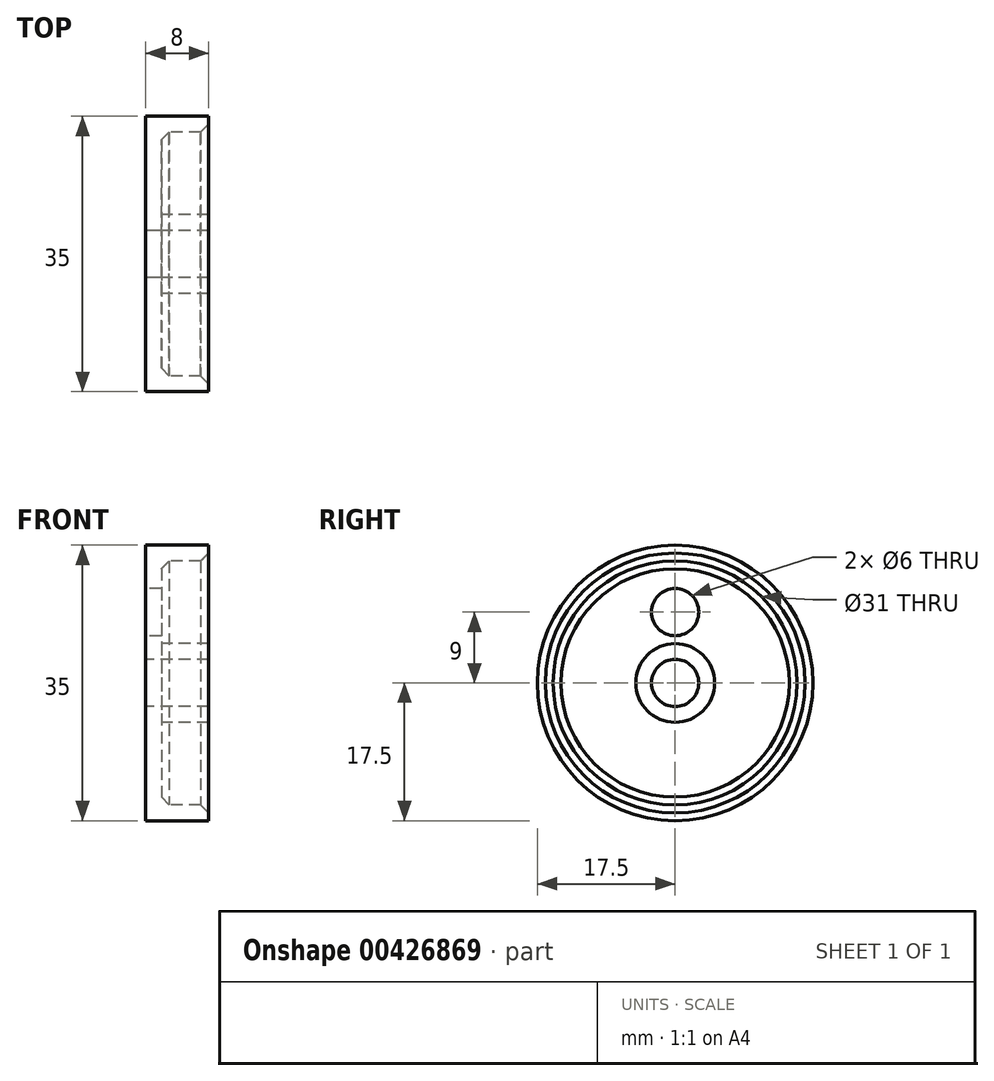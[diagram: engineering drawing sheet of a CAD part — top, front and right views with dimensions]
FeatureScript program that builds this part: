
annotation { "Feature Type Name" : "Feature", "Feature Type Description" : "" }
export const myFeature = defineFeature(function(context is Context, id is Id, definition is map)
    precondition{}
    {
        {
            var Q0;
            Q0=qCreatedBy(makeId("Top.planeOp"),FACE);
            var sketch = newSketch(context, id + "F0", { "sketchPlane" : qUnion([Q0])});
            skLineSegment(sketch, "E0.bottom", {"start": v(0, 0) * mm, "end": v(8, 0) * mm});
            skLineSegment(sketch, "E0.top", {"start": v(0, 17.5) * mm, "end": v(8, 17.5) * mm});
            skLineSegment(sketch, "E0.left", {"start": v(0, 0) * mm, "end": v(0, 17.5) * mm});
            skLineSegment(sketch, "E0.right", {"start": v(8, 0) * mm, "end": v(8, 17.5) * mm});
            skSolve(sketch);
        }
        {
            var Q0;
            Q0 = qSketchRegion(id + "F0", true);
            var Q1;
            Q1=sQuery(id+"F0.wireOp",EDGE,"E0.bottom");
            revolve(context, id + "F1", {"entities" : qUnion([Q0]), "axis" : qUnion([Q1]), "revolveType" : RevolveType.FULL});
        }
        {
            var Q0;
            Q0=qCreatedBy(makeId("Right.planeOp"),FACE);
            var sketch = newSketch(context, id + "F2", { "sketchPlane" : qUnion([Q0])});
            skPoint(sketch, "E1", {"position": v(0, 0) * mm});
            skSolve(sketch);
        }
        {
            var Q0;
            Q0=sQuery(id+"F2.wireOp",VERTEX,"E1");
            var Q1;
            Q1=makeQuery(id+"F1.opRevolve","SWEPT_BODY",BODY,{"disambiguationData":[OSD([sQuery(id+"F0.wireOp",EDGE,"E0.bottom"),sQuery(id+"F0.wireOp",EDGE,"E0.top"),sQuery(id+"F0.wireOp",EDGE,"E0.left"),sQuery(id+"F0.wireOp",EDGE,"E0.right")])]});
            hole(context, id + "F3", {"style" : HoleStyle.SIMPLE, "endStyle" : HoleEndStyle.THROUGH, "oppositeDirection" : true, "holeDiameter" : 6 * mm, "isTappedThrough" : true, "tappedDepth" : 12 * mm, "tapClearance" : 3, "locations" : qUnion([Q0]), "scope" : qUnion([Q1])});
        }
        {
            var Q0;
            Q0=makeQuery(id+"F1.opRevolve","SWEPT_FACE",FACE,{"disambiguationData":[OSD([sQuery(id+"F0.wireOp",EDGE,"E0.right")])]});
            shell(context, id + "F4", {"entities" : qUnion([Q0]), "thickness" : 2 * mm});
        }
        {
            var Q0;
            Q0=makeQuery(id+"F4.opShell","OFFSET_FACE",FACE,{"disambiguationData":[OSD([sQuery(id+"F0.wireOp",EDGE,"E0.top")])]});
            chamfer(context, id + "F5", {"entities" : qUnion([Q0]), "width" : 1 * mm, "tangentPropagation" : true});
        }
        {
            var Q0;
            Q0=qCreatedBy(makeId("Right.planeOp"),FACE);
            var sketch = newSketch(context, id + "F6", { "sketchPlane" : qUnion([Q0])});
            skPoint(sketch, "E2", {"position": v(22.4, 8.83) * mm});
            skCircle(sketch, "E3", {"center": v(0, 9) * mm, "radius": 2.06 * mm});
            skSolve(sketch);
        }
        {
            var Q0;
            Q0=sQuery(id+"F6.wireOp",VERTEX,"E3.center");
            var Q1;
            Q1=makeQuery(id+"F1.opRevolve","SWEPT_BODY",BODY,{"disambiguationData":[OSD([sQuery(id+"F0.wireOp",EDGE,"E0.bottom"),sQuery(id+"F0.wireOp",EDGE,"E0.top"),sQuery(id+"F0.wireOp",EDGE,"E0.left"),sQuery(id+"F0.wireOp",EDGE,"E0.right")])]});
            hole(context, id + "F7", {"style" : HoleStyle.SIMPLE, "endStyle" : HoleEndStyle.THROUGH, "oppositeDirection" : true, "holeDiameter" : 6 * mm, "isTappedThrough" : true, "tappedDepth" : 12 * mm, "tapClearance" : 3, "locations" : qUnion([Q0]), "scope" : qUnion([Q1])});
        }
    });
